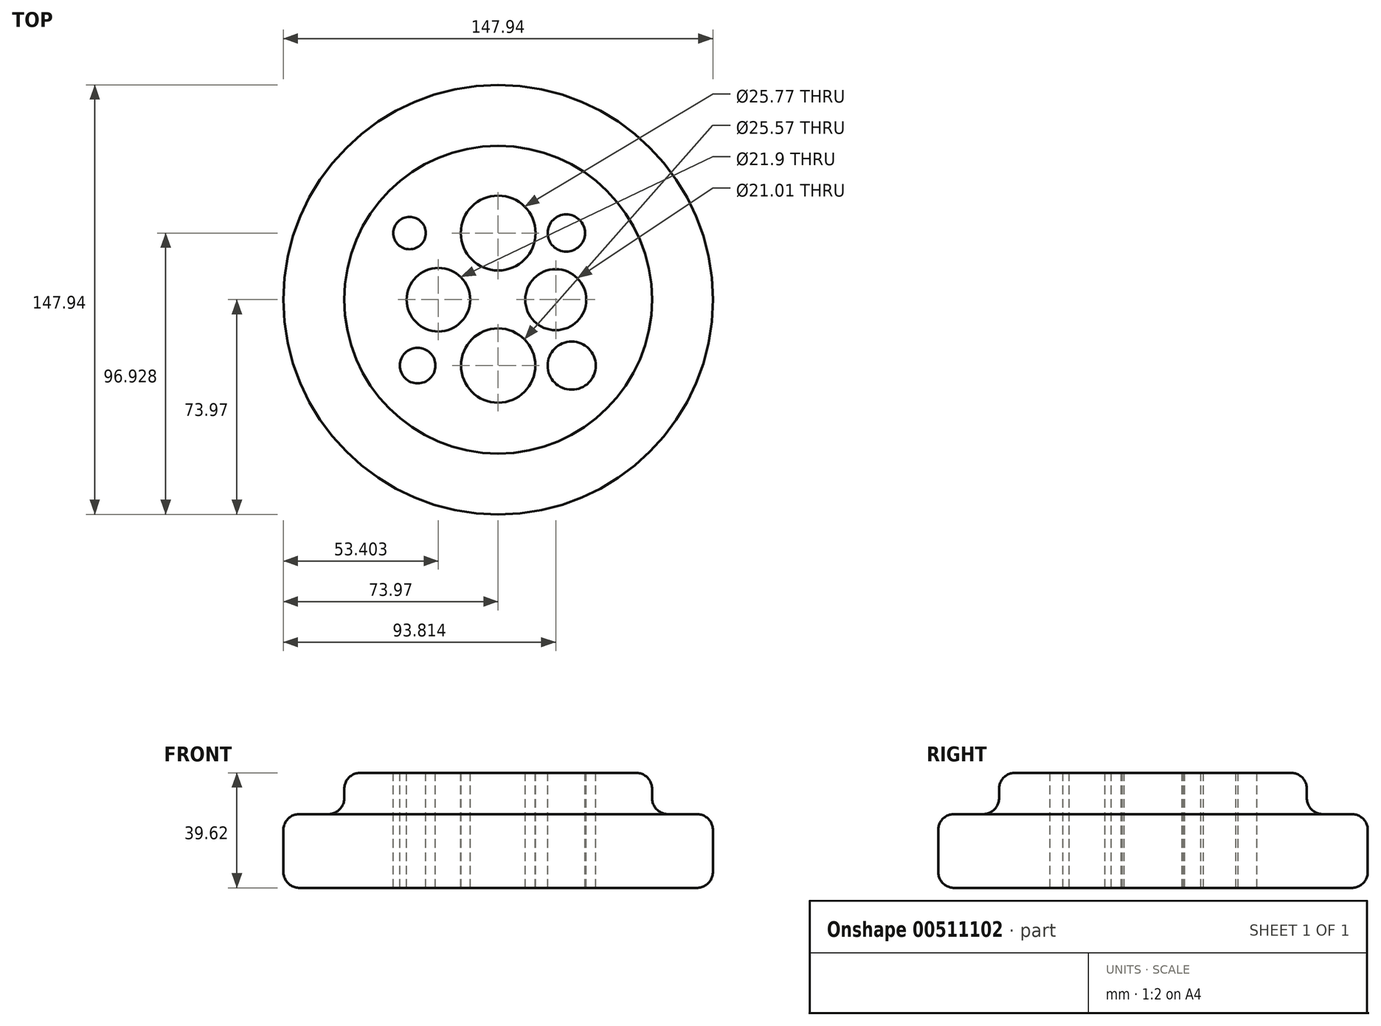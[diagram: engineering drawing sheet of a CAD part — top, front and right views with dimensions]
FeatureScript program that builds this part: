
annotation { "Feature Type Name" : "Feature", "Feature Type Description" : "" }
export const myFeature = defineFeature(function(context is Context, id is Id, definition is map)
    precondition{}
    {
        {
            var Q0;
            Q0=qCreatedBy(makeId("Top.planeOp"),FACE);
            var sketch = newSketch(context, id + "F0", { "sketchPlane" : qUnion([Q0])});
            skCircle(sketch, "E0", {"center": v(0, 0) * mm, "radius": 73.97 * mm});
            skSolve(sketch);
        }
        {
            var Q0;
            Q0=makeQuery(id+"F0.imprint","IMPRINT",FACE,{"disambiguationData":[TD([[makeQuery(id+"F0.imprint","IMPRINT",EDGE,{"derivedFrom":sQuery(id+"F0.wireOp",EDGE,"E0")}),1.0]])]});
            var sketch = newSketch(context, id + "F1", { "sketchPlane" : qUnion([Q0])});
            skCircle(sketch, "E1", {"center": v(0, 0) * mm, "radius": 53 * mm});
            skSolve(sketch);
        }
        {
            var Q0;
            Q0=makeQuery(id+"F0.imprint","IMPRINT",FACE,{"disambiguationData":[TD([[makeQuery(id+"F0.imprint","IMPRINT",EDGE,{"derivedFrom":sQuery(id+"F0.wireOp",EDGE,"E0")}),1.0]])]});
            extrude(context, id + "F2", {"entities" : qUnion([Q0]), "depth" : 25.4 * mm});
        }
        {
            var Q0;
            Q0=makeQuery(id+"F1.imprint","IMPRINT",FACE,{"disambiguationData":[TD([[makeQuery(id+"F1.imprint","IMPRINT",EDGE,{"derivedFrom":sQuery(id+"F1.wireOp",EDGE,"E1")}),1.0]])]});
            extrude(context, id + "F3", {"entities" : qUnion([Q0]), "operationType" : NewBodyOperationType.ADD, "depth" : 39.62 * mm});
        }
        {
            var Q0;
            Q0=makeQuery(id+"F2.opExtrude","CAP_FACE",FACE,{"disambiguationData":[OSD([sQuery(id+"F0.wireOp",EDGE,"E0")])],"isStart":true});
            var sketch = newSketch(context, id + "F4", { "sketchPlane" : qUnion([Q0])});
            skCircle(sketch, "E2", {"center": v(0, 0) * mm, "radius": 73.97 * mm});
            skSolve(sketch);
        }
        {
            var Q0;
            Q0=makeQuery(id+"F3.opExtrude","SWEPT_FACE",FACE,{"disambiguationData":[OSD([sQuery(id+"F1.wireOp",EDGE,"E1")])]});
            var Q1;
            Q1=makeQuery(id+"F2.opExtrude","SWEPT_FACE",FACE,{"disambiguationData":[OSD([sQuery(id+"F0.wireOp",EDGE,"E0")])]});
            fillet(context, id + "F5", {"entities" : qUnion([Q0, Q1]), "radius" : 5.52 * mm, "tangentPropagation" : true, "allowEdgeOverflow" : false});
        }
        {
            var Q0;
            Q0=makeQuery(id+"F3.opExtrude","CAP_FACE",FACE,{"disambiguationData":[OSD([sQuery(id+"F1.wireOp",EDGE,"E1")])],"isStart":false});
            var sketch = newSketch(context, id + "F6", { "sketchPlane" : qUnion([Q0])});
            skCircle(sketch, "E3", {"center": v(0, 22.96) * mm, "radius": 12.88 * mm});
            skCircle(sketch, "E4", {"center": v(0, -22.7) * mm, "radius": 12.78 * mm});
            skCircle(sketch, "E5", {"center": v(-20.57, 0) * mm, "radius": 10.95 * mm});
            skCircle(sketch, "E6", {"center": v(18.47, 0) * mm, "radius": 11.61 * mm});
            skCircle(sketch, "E7", {"center": v(-27.73, -22.7) * mm, "radius": 6.13 * mm});
            skCircle(sketch, "E8", {"center": v(-30.51, 22.96) * mm, "radius": 5.59 * mm});
            skCircle(sketch, "E9", {"center": v(23.47, 22.96) * mm, "radius": 6.41 * mm});
            skCircle(sketch, "E10", {"center": v(25.34, -22.7) * mm, "radius": 8.3 * mm});
            skSolve(sketch);
        }
        {
            var Q0;
            Q0=makeQuery(id+"F6.imprint","IMPRINT",FACE,{"disambiguationData":[TD([[makeQuery(id+"F6.imprint","IMPRINT",EDGE,{"derivedFrom":sQuery(id+"F6.wireOp",EDGE,"E3")}),1.0]])]});
            var Q1;
            Q1=makeQuery(id+"F6.imprint","IMPRINT",FACE,{"disambiguationData":[TD([[makeQuery(id+"F6.imprint","IMPRINT",EDGE,{"derivedFrom":sQuery(id+"F6.wireOp",EDGE,"E4")}),1.0]])]});
            var Q2;
            Q2=makeQuery(id+"F6.imprint","IMPRINT",FACE,{"disambiguationData":[TD([[makeQuery(id+"F6.imprint","IMPRINT",EDGE,{"derivedFrom":sQuery(id+"F6.wireOp",EDGE,"E5")}),1.0]])]});
            var Q3;
            Q3=makeQuery(id+"F6.imprint","IMPRINT",FACE,{"disambiguationData":[TD([[makeQuery(id+"F6.imprint","IMPRINT",EDGE,{"derivedFrom":sQuery(id+"F6.wireOp",EDGE,"E7")}),1.0]])]});
            var Q4;
            Q4=makeQuery(id+"F6.imprint","IMPRINT",FACE,{"disambiguationData":[TD([[makeQuery(id+"F6.imprint","IMPRINT",EDGE,{"derivedFrom":sQuery(id+"F6.wireOp",EDGE,"E8")}),1.0]])]});
            var Q5;
            Q5=makeQuery(id+"F6.imprint","IMPRINT",FACE,{"disambiguationData":[TD([[makeQuery(id+"F6.imprint","IMPRINT",EDGE,{"derivedFrom":sQuery(id+"F6.wireOp",EDGE,"E9")}),1.0]])]});
            var Q6;
            Q6=makeQuery(id+"F6.imprint","IMPRINT",FACE,{"disambiguationData":[TD([[makeQuery(id+"F6.imprint","IMPRINT",EDGE,{"derivedFrom":sQuery(id+"F6.wireOp",EDGE,"E10")}),1.0]])]});
            extrude(context, id + "F7", {"entities" : qUnion([Q0, Q1, Q2, Q3, Q4, Q5, Q6]), "operationType" : NewBodyOperationType.REMOVE, "oppositeDirection" : true, "depth" : 70.87 * mm, "offsetDistance" : 25.4 * mm});
        }
        {
            var Q0;
            Q0=makeQuery(id+"F3.opExtrude","CAP_FACE",FACE,{"disambiguationData":[OSD([sQuery(id+"F1.wireOp",EDGE,"E1")])],"isStart":false});
            var sketch = newSketch(context, id + "F8", { "sketchPlane" : qUnion([Q0])});
            skCircle(sketch, "E11", {"center": v(19.84, 0) * mm, "radius": 10.5 * mm});
            skSolve(sketch);
        }
        {
            var Q0;
            Q0=makeQuery(id+"F8.imprint","IMPRINT",FACE,{"disambiguationData":[TD([[makeQuery(id+"F8.imprint","IMPRINT",EDGE,{"derivedFrom":sQuery(id+"F8.wireOp",EDGE,"E11")}),1.0]])]});
            extrude(context, id + "F9", {"entities" : qUnion([Q0]), "operationType" : NewBodyOperationType.REMOVE, "oppositeDirection" : true, "depth" : 50.55 * mm, "offsetDistance" : 25.4 * mm});
        }
    });
